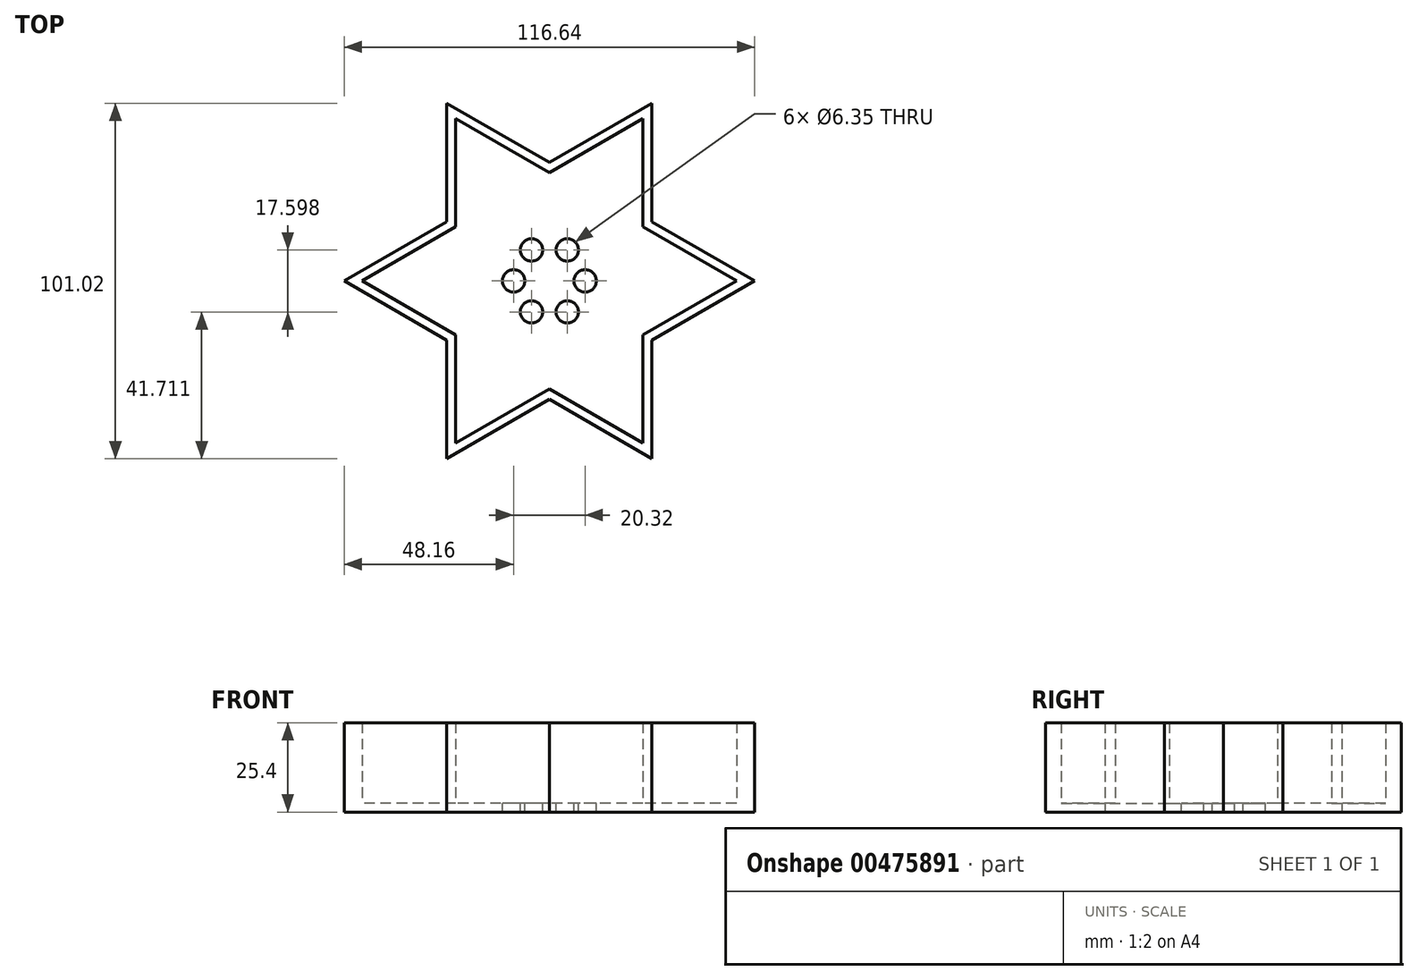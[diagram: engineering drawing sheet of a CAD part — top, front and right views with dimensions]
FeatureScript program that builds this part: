
annotation { "Feature Type Name" : "Feature", "Feature Type Description" : "" }
export const myFeature = defineFeature(function(context is Context, id is Id, definition is map)
    precondition{}
    {
        {
            var Q0;
            Q0=qCreatedBy(makeId("Top.planeOp"),FACE);
            var sketch = newSketch(context, id + "F0", { "sketchPlane" : qUnion([Q0])});
            skCircle(sketch, "E0.cCircle", {"center": v(0, 0) * mm, "radius": 29.16 * mm, "construction": true});
            skLineSegment(sketch, "E0.0", {"start": v(29.16, 50.5) * mm, "end": v(29.16, -50.5) * mm, "construction": true});
            skLineSegment(sketch, "E0.1", {"start": v(29.16, -50.5) * mm, "end": v(-58.32, 0) * mm, "construction": true});
            skLineSegment(sketch, "E0.2", {"start": v(-58.32, 0) * mm, "end": v(29.16, 50.5) * mm, "construction": true});
            skPoint(sketch, "E0.0.midPoint", {"position": v(29.16, 0) * mm});
            skLineSegment(sketch, "E1.0", {"start": v(-29.16, -50.5) * mm, "end": v(-29.16, 50.5) * mm, "construction": true});
            skLineSegment(sketch, "E1.1", {"start": v(-29.16, 50.5) * mm, "end": v(58.32, 0) * mm, "construction": true});
            skLineSegment(sketch, "E1.2", {"start": v(58.32, 0) * mm, "end": v(-29.16, -50.5) * mm, "construction": true});
            skPoint(sketch, "E1.0.midPoint", {"position": v(-29.16, 0) * mm});
            skPoint(sketch, "E2", {"position": v(-29.16, -16.84) * mm});
            skPoint(sketch, "E3", {"position": v(0, -33.67) * mm});
            skPoint(sketch, "E4", {"position": v(29.16, -16.84) * mm});
            skPoint(sketch, "E5", {"position": v(29.16, 16.84) * mm});
            skPoint(sketch, "E6", {"position": v(0, 33.67) * mm});
            skPoint(sketch, "E7", {"position": v(-29.16, 16.84) * mm});
            skLineSegment(sketch, "E8", {"start": v(-29.16, -16.84) * mm, "end": v(-58.32, 0) * mm});
            skLineSegment(sketch, "E9", {"start": v(-29.16, 16.84) * mm, "end": v(-58.32, 0) * mm});
            skLineSegment(sketch, "E10", {"start": v(-29.16, 16.84) * mm, "end": v(-29.16, 50.5) * mm});
            skLineSegment(sketch, "E11", {"start": v(-29.16, 50.5) * mm, "end": v(0, 33.67) * mm});
            skLineSegment(sketch, "E12", {"start": v(0, 33.67) * mm, "end": v(29.16, 50.5) * mm});
            skLineSegment(sketch, "E13", {"start": v(29.16, 50.5) * mm, "end": v(29.16, 16.84) * mm});
            skLineSegment(sketch, "E14", {"start": v(29.16, 16.84) * mm, "end": v(58.32, 0) * mm});
            skLineSegment(sketch, "E15", {"start": v(58.32, 0) * mm, "end": v(29.16, -16.84) * mm});
            skLineSegment(sketch, "E16", {"start": v(29.16, -16.84) * mm, "end": v(29.16, -50.5) * mm});
            skLineSegment(sketch, "E17", {"start": v(29.16, -50.5) * mm, "end": v(0, -33.67) * mm});
            skLineSegment(sketch, "E18", {"start": v(0, -33.67) * mm, "end": v(-29.16, -50.5) * mm});
            skLineSegment(sketch, "E19", {"start": v(-29.16, -50.5) * mm, "end": v(-29.16, -16.84) * mm});
            skSolve(sketch);
        }
        {
            var Q0;
            Q0=makeQuery(id+"F0.imprint","IMPRINT",FACE,{"disambiguationData":[TD([[makeQuery(id+"F0.imprint","IMPRINT",EDGE,{"derivedFrom":sQuery(id+"F0.wireOp",EDGE,"E8")}),-1.0]])]});
            extrude(context, id + "F1", {"entities" : qUnion([Q0]), "depth" : 25.4 * mm});
        }
        {
            var Q0;
            Q0=makeQuery(id+"F1.opExtrude","CAP_FACE",FACE,{"disambiguationData":[OSD([sQuery(id+"F0.wireOp",EDGE,"E8"),sQuery(id+"F0.wireOp",EDGE,"E9"),sQuery(id+"F0.wireOp",EDGE,"E10"),sQuery(id+"F0.wireOp",EDGE,"E11"),sQuery(id+"F0.wireOp",EDGE,"E12"),sQuery(id+"F0.wireOp",EDGE,"E13"),sQuery(id+"F0.wireOp",EDGE,"E14"),sQuery(id+"F0.wireOp",EDGE,"E15"),sQuery(id+"F0.wireOp",EDGE,"E16"),sQuery(id+"F0.wireOp",EDGE,"E17"),sQuery(id+"F0.wireOp",EDGE,"E18"),sQuery(id+"F0.wireOp",EDGE,"E19")])],"isStart":false});
            shell(context, id + "F2", {"entities" : qUnion([Q0]), "thickness" : 2.54 * mm});
        }
        {
            var Q0;
            Q0=makeQuery(id+"F2.opShell","OFFSET_FACE",FACE,{"disambiguationData":[OSD([sQuery(id+"F0.wireOp",EDGE,"E8"),sQuery(id+"F0.wireOp",EDGE,"E9"),sQuery(id+"F0.wireOp",EDGE,"E10"),sQuery(id+"F0.wireOp",EDGE,"E11"),sQuery(id+"F0.wireOp",EDGE,"E12"),sQuery(id+"F0.wireOp",EDGE,"E13"),sQuery(id+"F0.wireOp",EDGE,"E14"),sQuery(id+"F0.wireOp",EDGE,"E15"),sQuery(id+"F0.wireOp",EDGE,"E16"),sQuery(id+"F0.wireOp",EDGE,"E17"),sQuery(id+"F0.wireOp",EDGE,"E18"),sQuery(id+"F0.wireOp",EDGE,"E19")])]});
            var sketch = newSketch(context, id + "F3", { "sketchPlane" : qUnion([Q0])});
            skLineSegment(sketch, "E20", {"start": v(26.62, 46.1) * mm, "end": v(0, 0) * mm, "construction": true});
            skLineSegment(sketch, "E21", {"start": v(0, 0) * mm, "end": v(53.24, 0) * mm, "construction": true});
            skLineSegment(sketch, "E22", {"start": v(53.24, 0) * mm, "end": v(-53.24, 0) * mm, "construction": true});
            skLineSegment(sketch, "E23", {"start": v(-53.24, 0) * mm, "end": v(0, 0) * mm, "construction": true});
            skLineSegment(sketch, "E24", {"start": v(-26.62, 46.1) * mm, "end": v(26.62, -46.1) * mm, "construction": true});
            skLineSegment(sketch, "E25", {"start": v(26.62, -46.1) * mm, "end": v(0, 0) * mm, "construction": true});
            skLineSegment(sketch, "E26", {"start": v(-26.62, -46.1) * mm, "end": v(0, 0) * mm, "construction": true});
            skLineSegment(sketch, "E27", {"start": v(0, 0) * mm, "end": v(5.08, 8.8) * mm, "construction": true});
            skLineSegment(sketch, "E28", {"start": v(0, 0) * mm, "end": v(10.16, 0) * mm, "construction": true});
            skLineSegment(sketch, "E29", {"start": v(0, 0) * mm, "end": v(5.08, -8.8) * mm, "construction": true});
            skLineSegment(sketch, "E30", {"start": v(0, 0) * mm, "end": v(-10.16, 0) * mm, "construction": true});
            skLineSegment(sketch, "E31", {"start": v(0, 0) * mm, "end": v(-5.08, 8.8) * mm, "construction": true});
            skCircle(sketch, "E32", {"center": v(5.08, 8.8) * mm, "radius": 3.18 * mm});
            skCircle(sketch, "E33", {"center": v(10.16, 0) * mm, "radius": 3.18 * mm});
            skCircle(sketch, "E34", {"center": v(5.08, -8.8) * mm, "radius": 3.18 * mm});
            skLineSegment(sketch, "E35", {"start": v(0, 0) * mm, "end": v(-5.08, -8.8) * mm, "construction": true});
            skCircle(sketch, "E36", {"center": v(-5.08, -8.8) * mm, "radius": 3.18 * mm});
            skCircle(sketch, "E37", {"center": v(-10.16, 0) * mm, "radius": 3.18 * mm});
            skCircle(sketch, "E38", {"center": v(-5.08, 8.8) * mm, "radius": 3.18 * mm});
            skSolve(sketch);
        }
        {
            var Q0;
            Q0 = qSketchRegion(id + "F3", true);
            extrude(context, id + "F4", {"entities" : qUnion([Q0]), "operationType" : NewBodyOperationType.REMOVE, "oppositeDirection" : true, "depth" : 25.4 * mm, "offsetDistance" : 25.4 * mm});
        }
    });
